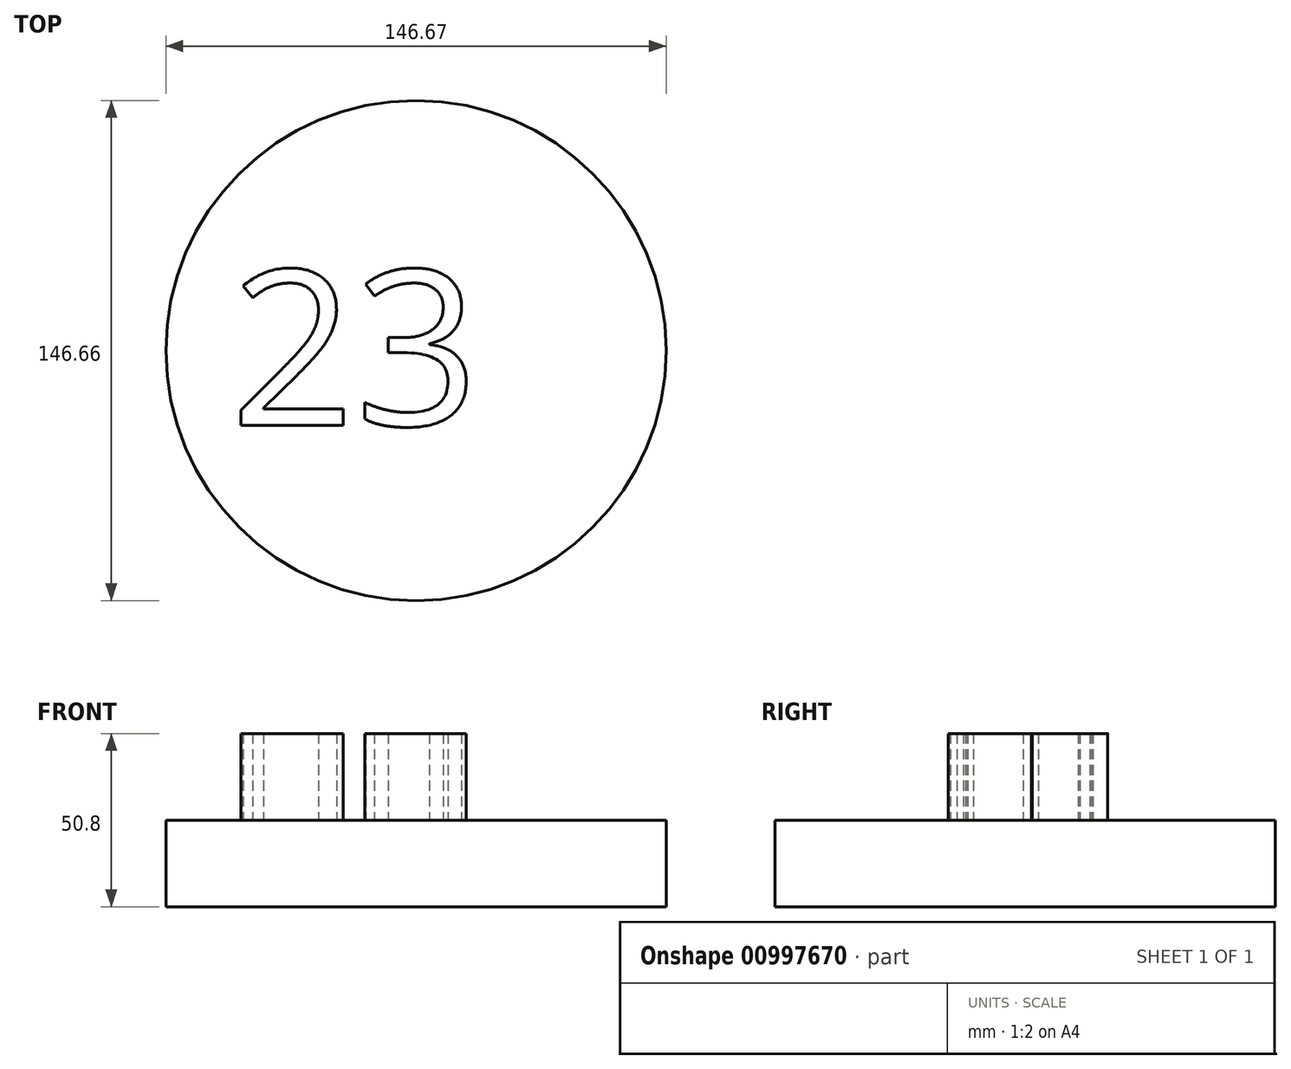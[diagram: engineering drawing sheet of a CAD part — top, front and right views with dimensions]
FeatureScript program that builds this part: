
annotation { "Feature Type Name" : "Feature", "Feature Type Description" : "" }
export const myFeature = defineFeature(function(context is Context, id is Id, definition is map)
    precondition{}
    {
        {
            var Q0;
            Q0=qCreatedBy(makeId("Top.planeOp"),FACE);
            var sketch = newSketch(context, id + "F0", { "sketchPlane" : qUnion([Q0])});
            skCircle(sketch, "E0", {"center": v(2.29, 0) * mm, "radius": 73.33 * mm});
            skSolve(sketch);
        }
        {
            var Q0;
            Q0=makeQuery(id+"F0.imprint","IMPRINT",FACE,{"disambiguationData":[TD([[makeQuery(id+"F0.imprint","IMPRINT",EDGE,{"derivedFrom":sQuery(id+"F0.wireOp",EDGE,"E0")}),1.0]])]});
            extrude(context, id + "F1", {"entities" : qUnion([Q0]), "depth" : 25.4 * mm, "offsetDistance" : 25.4 * mm});
        }
        {
            var Q0;
            Q0=makeQuery(id+"F1.opExtrude","CAP_FACE",FACE,{"disambiguationData":[OSD([sQuery(id+"F0.wireOp",EDGE,"E0")])],"isStart":false});
            var sketch = newSketch(context, id + "F2", { "sketchPlane" : qUnion([Q0])});
            skText(sketch, "E1", { "text": "23", "fontName": "OpenSans-Regular.ttf"});
            const initialGuessF2  = {"E1": [-0.05211, -0.02194, 1, 0, 0.04588]};
            skSetInitialGuess(sketch, initialGuessF2);
            skSolve(sketch);
        }
        {
            var Q0;
            Q0 = qSketchRegion(id + "F2", true);
            extrude(context, id + "F3", {"entities" : qUnion([Q0]), "operationType" : NewBodyOperationType.ADD, "depth" : 25.4 * mm, "offsetDistance" : 25.4 * mm});
        }
    });
